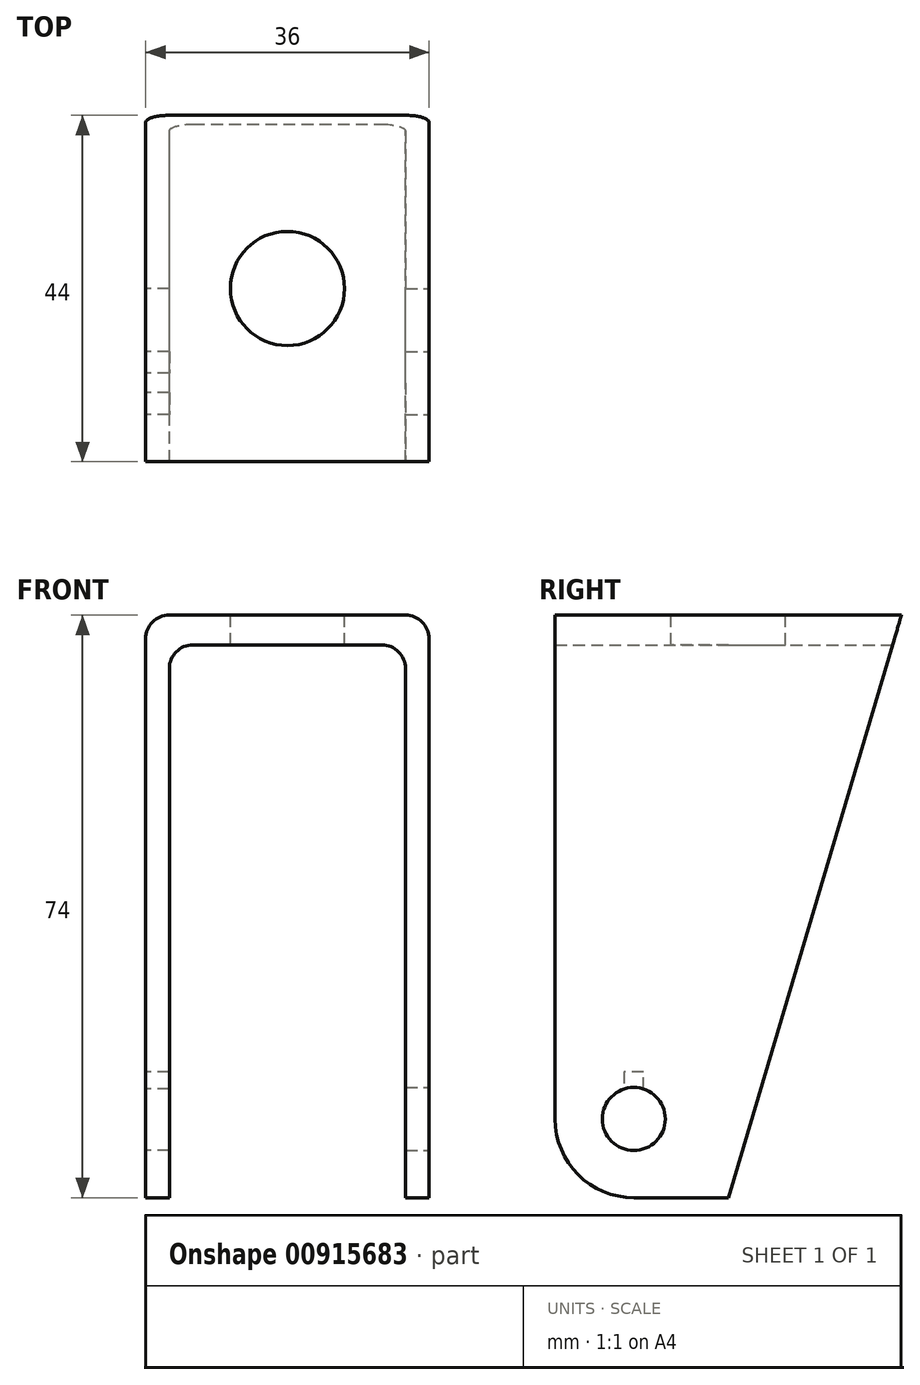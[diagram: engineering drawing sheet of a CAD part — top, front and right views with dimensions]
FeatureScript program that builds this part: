
annotation { "Feature Type Name" : "Feature", "Feature Type Description" : "" }
export const myFeature = defineFeature(function(context is Context, id is Id, definition is map)
    precondition{}
    {
        {
            var Q0;
            Q0=qCreatedBy(makeId("Front.planeOp"),FACE);
            var sketch = newSketch(context, id + "F0", { "sketchPlane" : qUnion([Q0])});
            skLineSegment(sketch, "E0", {"start": v(0, 0) * mm, "end": v(0, 74) * mm});
            skLineSegment(sketch, "E1", {"start": v(0, 74) * mm, "end": v(36, 74) * mm});
            skLineSegment(sketch, "E2", {"start": v(36, 74) * mm, "end": v(36, 0) * mm});
            skLineSegment(sketch, "E3", {"start": v(36, 0) * mm, "end": v(33, 0) * mm});
            skLineSegment(sketch, "E4", {"start": v(33, 0) * mm, "end": v(33, 70.22) * mm});
            skLineSegment(sketch, "E5", {"start": v(33, 70.22) * mm, "end": v(3, 70.22) * mm});
            skLineSegment(sketch, "E6", {"start": v(3, 70.22) * mm, "end": v(3, 0) * mm});
            skLineSegment(sketch, "E7", {"start": v(3, 0) * mm, "end": v(0, 0) * mm});
            skSolve(sketch);
        }
        {
            var Q0;
            Q0 = qSketchRegion(id + "F0", true);
            extrude(context, id + "F1", {"entities" : qUnion([Q0]), "depth" : 44 * mm, "offsetDistance" : 25 * mm});
        }
        {
            var Q0;
            Q0=makeQuery(id+"F1.opExtrude","SWEPT_FACE",FACE,{"disambiguationData":[OSD([sQuery(id+"F0.wireOp",EDGE,"E2")])]});
            var sketch = newSketch(context, id + "F2", { "sketchPlane" : qUnion([Q0])});
            skLineSegment(sketch, "E8", {"start": v(-22, 0) * mm, "end": v(0, 74) * mm});
            skCircle(sketch, "E9", {"center": v(-34, 10) * mm, "radius": 4 * mm});
            skSolve(sketch);
        }
        {
            var Q0;
            Q0=makeQuery(id+"F2.imprint","IMPRINT",FACE,{"disambiguationData":[TD([[makeQuery(id+"F2.imprint","IMPRINT",EDGE,{"derivedFrom":sQuery(id+"F2.wireOp",EDGE,"E9")}),1.0]])]});
            extrude(context, id + "F3", {"entities" : qUnion([Q0]), "operationType" : NewBodyOperationType.REMOVE, "oppositeDirection" : true, "depth" : 25 * mm, "offsetDistance" : 25 * mm});
        }
        {
            var Q0;
            {var subQ0=sQuery(id+"F2.wireOp",EDGE,"E8");Q0=makeQuery(id+"F2.imprint","IMPRINT",FACE,{"disambiguationData":[TD([[makeQuery(id+"F2.imprint","IMPRINT",EDGE,{"derivedFrom":subQ0}),-1.0]])]});}
            extrude(context, id + "F4", {"entities" : qUnion([Q0]), "operationType" : NewBodyOperationType.REMOVE, "oppositeDirection" : true, "depth" : 25 * mm, "offsetDistance" : 25 * mm});
        }
        {
            var Q0;
            Q0=makeQuery(id+"F1.opExtrude","SWEPT_FACE",FACE,{"disambiguationData":[OSD([sQuery(id+"F0.wireOp",EDGE,"E0")])]});
            var sketch = newSketch(context, id + "F5", { "sketchPlane" : qUnion([Q0])});
            skLineSegment(sketch, "E10", {"start": v(0, 74) * mm, "end": v(22, 0) * mm});
            skCircle(sketch, "E11", {"center": v(34, 10) * mm, "radius": 4 * mm});
            skSolve(sketch);
        }
        {
            var Q0;
            {var subQ0=sQuery(id+"F5.wireOp",EDGE,"E10");Q0=makeQuery(id+"F5.imprint","IMPRINT",FACE,{"disambiguationData":[TD([[makeQuery(id+"F5.imprint","IMPRINT",EDGE,{"derivedFrom":subQ0}),-1.0]])]});}
            extrude(context, id + "F6", {"entities" : qUnion([Q0]), "operationType" : NewBodyOperationType.REMOVE, "oppositeDirection" : true, "depth" : 25 * mm, "offsetDistance" : 25 * mm});
        }
        {
            var Q0;
            Q0=makeQuery(id+"F5.imprint","IMPRINT",FACE,{"disambiguationData":[TD([[makeQuery(id+"F5.imprint","IMPRINT",EDGE,{"derivedFrom":sQuery(id+"F5.wireOp",EDGE,"E11")}),1.0]])]});
            extrude(context, id + "F7", {"entities" : qUnion([Q0]), "operationType" : NewBodyOperationType.REMOVE, "oppositeDirection" : true, "depth" : 25 * mm, "offsetDistance" : 25 * mm});
        }
        {
            var Q0;
            Q0=makeQuery(id+"F1.opExtrude","SWEPT_EDGE",EDGE,{"disambiguationData":[OSD([sQuery(id+"F0.wireOp",EDGE,"E1"),sQuery(id+"F0.wireOp",EDGE,"E2")])]});
            var Q1;
            Q1=makeQuery(id+"F1.opExtrude","SWEPT_EDGE",EDGE,{"disambiguationData":[OSD([sQuery(id+"F0.wireOp",EDGE,"E0"),sQuery(id+"F0.wireOp",EDGE,"E1")])]});
            var Q2;
            Q2=makeQuery(id+"F1.opExtrude","SWEPT_EDGE",EDGE,{"disambiguationData":[OSD([sQuery(id+"F0.wireOp",EDGE,"E4"),sQuery(id+"F0.wireOp",EDGE,"E5")])]});
            var Q3;
            Q3=makeQuery(id+"F1.opExtrude","SWEPT_EDGE",EDGE,{"disambiguationData":[OSD([sQuery(id+"F0.wireOp",EDGE,"E5"),sQuery(id+"F0.wireOp",EDGE,"E6")])]});
            fillet(context, id + "F8", {"entities" : qUnion([Q0, Q1, Q2, Q3]), "radius" : 3 * mm, "tangentPropagation" : true, "allowEdgeOverflow" : false});
        }
        {
            var Q0;
            Q0=makeQuery(id+"F1.opExtrude","SWEPT_FACE",FACE,{"disambiguationData":[OSD([sQuery(id+"F0.wireOp",EDGE,"E0")])]});
            var sketch = newSketch(context, id + "F9", { "sketchPlane" : qUnion([Q0])});
            skLineSegment(sketch, "E12", {"start": v(32.75, 13.8) * mm, "end": v(32.75, 16) * mm});
            skLineSegment(sketch, "E13", {"start": v(32.75, 16) * mm, "end": v(35.25, 16) * mm});
            skLineSegment(sketch, "E14", {"start": v(35.25, 16) * mm, "end": v(35.25, 13.8) * mm});
            skSolve(sketch);
        }
        {
            var Q0;
            {var subQ0=sQuery(id+"F9.wireOp",EDGE,"E12");Q0=makeQuery(id+"F9.imprint","IMPRINT",FACE,{"disambiguationData":[TD([[makeQuery(id+"F9.imprint","IMPRINT",EDGE,{"derivedFrom":subQ0}),-1.0]])]});}
            extrude(context, id + "F10", {"entities" : qUnion([Q0]), "operationType" : NewBodyOperationType.REMOVE, "oppositeDirection" : true, "depth" : 25 * mm, "offsetDistance" : 25 * mm});
        }
        {
            var Q0;
            Q0=makeQuery(id+"F6.boolean.opBoolean","COPY",EDGE,{"derivedFrom":makeQuery(id+"F6.opExtrude","SWEPT_EDGE",EDGE,{"disambiguationData":[OSD([sQuery(id+"F0.wireOp",EDGE,"E0"),sQuery(id+"F0.wireOp",EDGE,"E7"),sQuery(id+"F5.wireOp",EDGE,"E10")])]})});
            var Q1;
            Q1=makeQuery(id+"F1.opExtrude","CAP_EDGE",EDGE,{"disambiguationData":[OSD([sQuery(id+"F0.wireOp",EDGE,"E7")])],"isStart":false});
            var Q2;
            Q2=makeQuery(id+"F1.opExtrude","CAP_EDGE",EDGE,{"disambiguationData":[OSD([sQuery(id+"F0.wireOp",EDGE,"E3")])],"isStart":false});
            var Q3;
            Q3=makeQuery(id+"F4.boolean.opBoolean","COPY",EDGE,{"derivedFrom":makeQuery(id+"F4.opExtrude","SWEPT_EDGE",EDGE,{"disambiguationData":[OSD([sQuery(id+"F0.wireOp",EDGE,"E2"),sQuery(id+"F0.wireOp",EDGE,"E3"),sQuery(id+"F2.wireOp",EDGE,"E8")])]})});
            fillet(context, id + "F11", {"entities" : qUnion([Q0, Q1, Q2, Q3]), "radius" : 10 * mm, "tangentPropagation" : true, "allowEdgeOverflow" : false});
        }
        {
            var Q0;
            Q0=makeQuery(id+"F1.opExtrude","SWEPT_FACE",FACE,{"disambiguationData":[OSD([sQuery(id+"F0.wireOp",EDGE,"E1")])]});
            var sketch = newSketch(context, id + "F12", { "sketchPlane" : qUnion([Q0])});
            skCircle(sketch, "E15", {"center": v(18, -22) * mm, "radius": 7.25 * mm});
            skSolve(sketch);
        }
        {
            var Q0;
            Q0 = qSketchRegion(id + "F12", true);
            extrude(context, id + "F13", {"entities" : qUnion([Q0]), "operationType" : NewBodyOperationType.REMOVE, "oppositeDirection" : true, "depth" : 25 * mm, "offsetDistance" : 25 * mm});
        }
    });
